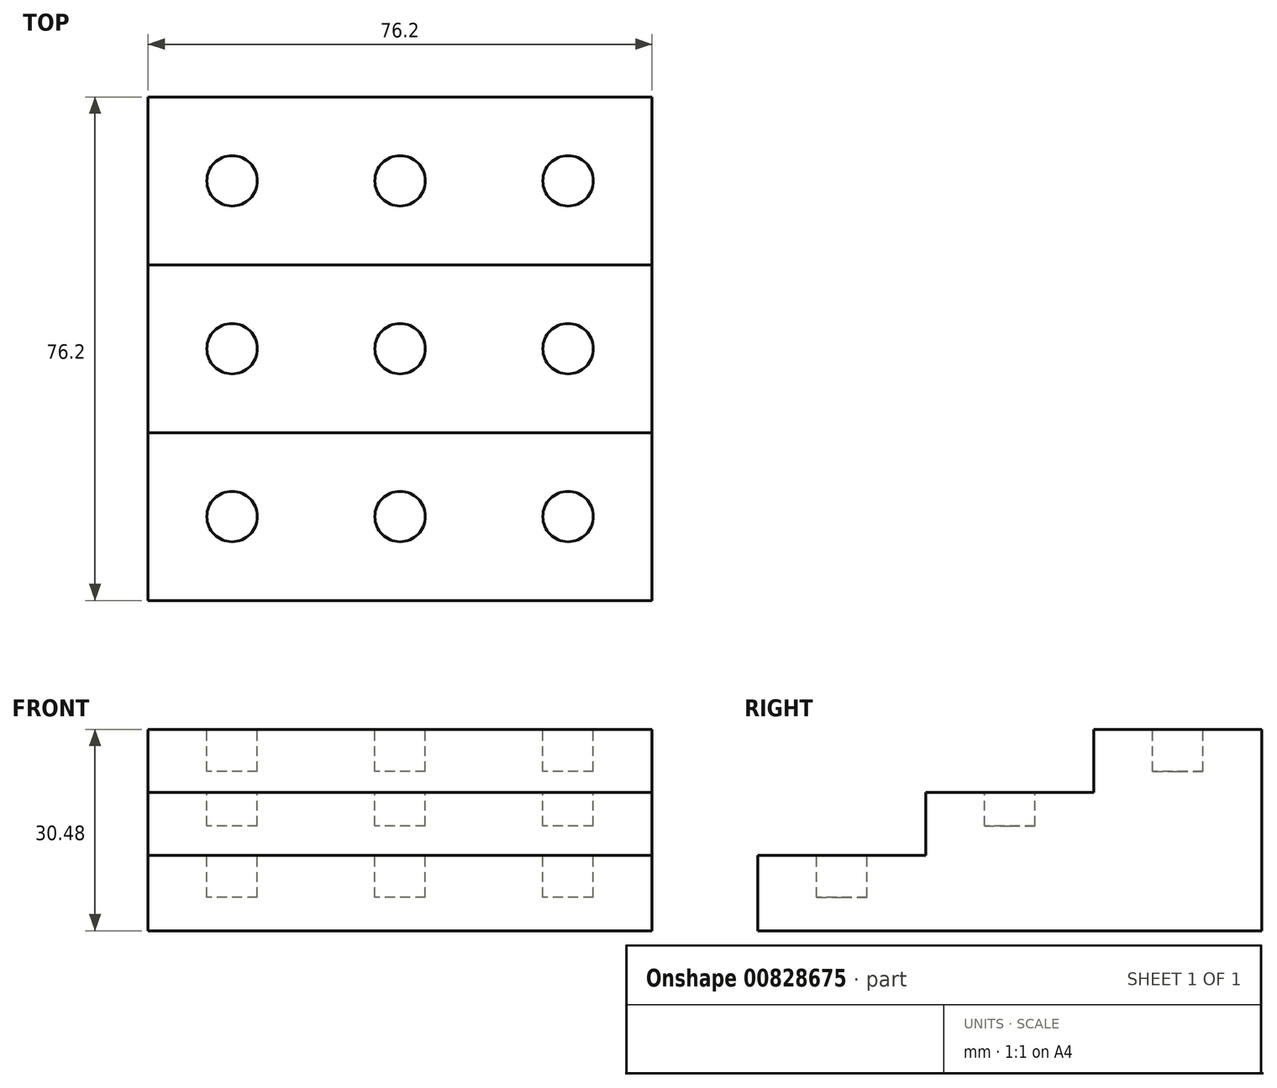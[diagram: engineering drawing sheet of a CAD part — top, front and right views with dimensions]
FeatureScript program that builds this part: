
annotation { "Feature Type Name" : "Feature", "Feature Type Description" : "" }
export const myFeature = defineFeature(function(context is Context, id is Id, definition is map)
    precondition{}
    {
        {
            var Q0;
            Q0=qCreatedBy(makeId("Top.planeOp"),FACE);
            var sketch = newSketch(context, id + "F0", { "sketchPlane" : qUnion([Q0])});
            skLineSegment(sketch, "E0", {"start": v(0, 0) * mm, "end": v(0, 25.4) * mm});
            skLineSegment(sketch, "E1", {"start": v(0, 25.4) * mm, "end": v(76.2, 25.4) * mm});
            skLineSegment(sketch, "E2", {"start": v(76.2, 25.4) * mm, "end": v(76.2, 0) * mm});
            skLineSegment(sketch, "E3", {"start": v(76.2, 0) * mm, "end": v(0, 0) * mm});
            skSolve(sketch);
        }
        {
            var Q0;
            Q0=qSketchRegion(id+"F0",true);
            extrude(context, id + "F1", {"entities" : qUnion([Q0]), "depth" : 11.43 * mm, "offsetDistance" : 25.4 * mm});
        }
        {
            var Q0;
            Q0=makeQuery(id+"F1.opExtrude","CAP_FACE",FACE,{"disambiguationData":[OSD([sQuery(id+"F0.wireOp",EDGE,"E0"),sQuery(id+"F0.wireOp",EDGE,"E1"),sQuery(id+"F0.wireOp",EDGE,"E2"),sQuery(id+"F0.wireOp",EDGE,"E3")])],"isStart":false});
            var sketch = newSketch(context, id + "F2", { "sketchPlane" : qUnion([Q0])});
            skCircle(sketch, "E4", {"center": v(12.7, 12.7) * mm, "radius": 3.81 * mm});
            skCircle(sketch, "E5", {"center": v(38.1, 12.7) * mm, "radius": 3.81 * mm});
            skCircle(sketch, "E6", {"center": v(63.5, 12.7) * mm, "radius": 3.81 * mm});
            skSolve(sketch);
        }
        {
            var Q0;
            Q0=qSketchRegion(id+"F2",true);
            extrude(context, id + "F3", {"entities" : qUnion([Q0]), "operationType" : NewBodyOperationType.REMOVE, "oppositeDirection" : true, "depth" : 6.35 * mm, "offsetDistance" : 25.4 * mm});
        }
        {
            var Q0;
            Q0=makeQuery(id+"F1.opExtrude","SWEPT_FACE",FACE,{"disambiguationData":[OSD([sQuery(id+"F0.wireOp",EDGE,"E1")])]});
            var sketch = newSketch(context, id + "F4", { "sketchPlane" : qUnion([Q0])});
            skSolve(sketch);
        }
        {
            var Q0;
            Q0 = qSketchRegion(id + "F4", true);
            var Q1;
            {var subQ0=sQuery(id+"F0.wireOp",EDGE,"E1");Q1=makeQuery(id+"F4.imprint","IMPRINT",FACE,{"disambiguationData":[TD([[makeQuery(id+"F4.imprint","IMPRINT",EDGE,{"derivedFrom":makeQuery(id+"F1.opExtrude","CAP_EDGE",EDGE,{"disambiguationData":[OSD([subQ0])],"isStart":true})}),-1.0]])]});}
            extrude(context, id + "F5", {"entities" : qUnion([Q0, Q1]), "operationType" : NewBodyOperationType.ADD, "depth" : 25.4 * mm, "offsetDistance" : 25.4 * mm});
        }
        {
            var Q0;
            {var subQ0=sQuery(id+"F0.wireOp",EDGE,"E1");Q0=makeQuery(id+"F5.boolean.opBoolean","MERGE",FACE,{"derivedFrom":[makeQuery(id+"F1.opExtrude","CAP_FACE",FACE,{"disambiguationData":[OSD([sQuery(id+"F0.wireOp",EDGE,"E0"),subQ0,sQuery(id+"F0.wireOp",EDGE,"E2"),sQuery(id+"F0.wireOp",EDGE,"E3")])],"isStart":false}),makeQuery(id+"F5.opExtrude","SWEPT_FACE",FACE,{"disambiguationData":[OSD([subQ0]),TDD([makeQuery(id+"F4.imprint","IMPRINT",EDGE,{"derivedFrom":makeQuery(id+"F1.opExtrude","CAP_EDGE",EDGE,{"disambiguationData":[OSD([subQ0])],"isStart":false})})])]})]});}
            var sketch = newSketch(context, id + "F6", { "sketchPlane" : qUnion([Q0])});
            skLineSegment(sketch, "E7", {"start": v(76.2, 25.4) * mm, "end": v(0, 25.4) * mm});
            skSolve(sketch);
        }
        {
            var Q0;
            Q0 = qSketchRegion(id + "F6", true);
            var Q1;
            {var subQ0=sQuery(id+"F6.wireOp",EDGE,"E7");Q1=makeQuery(id+"F6.imprint","IMPRINT",FACE,{"disambiguationData":[TD([[makeQuery(id+"F6.imprint","IMPRINT",EDGE,{"derivedFrom":subQ0}),-1.0]])]});}
            extrude(context, id + "F7", {"entities" : qUnion([Q0, Q1]), "operationType" : NewBodyOperationType.ADD, "depth" : 9.52 * mm, "offsetDistance" : 25.4 * mm});
        }
        {
            var Q0;
            {var subQ0=sQuery(id+"F0.wireOp",EDGE,"E1");Q0=makeQuery(id+"F7.boolean.opBoolean","MERGE",FACE,{"derivedFrom":[makeQuery(id+"F5.opExtrude","CAP_FACE",FACE,{"disambiguationData":[OSD([sQuery(id+"F0.wireOp",EDGE,"E0"),subQ0,sQuery(id+"F0.wireOp",EDGE,"E2")])],"isStart":false}),makeQuery(id+"F7.opExtrude","SWEPT_FACE",FACE,{"disambiguationData":[OSD([subQ0])]})]});}
            var sketch = newSketch(context, id + "F8", { "sketchPlane" : qUnion([Q0])});
            skSolve(sketch);
        }
        {
            var Q0;
            {var subQ0=sQuery(id+"F0.wireOp",EDGE,"E1");Q0=makeQuery(id+"F8.imprint","IMPRINT",FACE,{"disambiguationData":[TD([[makeQuery(id+"F8.imprint","IMPRINT",EDGE,{"derivedFrom":makeQuery(id+"F7.opExtrude","CAP_EDGE",EDGE,{"disambiguationData":[OSD([subQ0])],"isStart":false})}),1.0]])]});}
            extrude(context, id + "F9", {"entities" : qUnion([Q0]), "operationType" : NewBodyOperationType.ADD, "depth" : 25.4 * mm, "offsetDistance" : 25.4 * mm});
        }
        {
            var Q0;
            {var subQ0=sQuery(id+"F0.wireOp",EDGE,"E1");Q0=makeQuery(id+"F9.boolean.opBoolean","MERGE",FACE,{"derivedFrom":[makeQuery(id+"F7.opExtrude","CAP_FACE",FACE,{"disambiguationData":[OSD([sQuery(id+"F0.wireOp",EDGE,"E0"),subQ0,sQuery(id+"F0.wireOp",EDGE,"E2"),sQuery(id+"F6.wireOp",EDGE,"E7")])],"isStart":false}),makeQuery(id+"F9.opExtrude","SWEPT_FACE",FACE,{"disambiguationData":[OSD([subQ0]),TDD([makeQuery(id+"F8.imprint","IMPRINT",EDGE,{"derivedFrom":makeQuery(id+"F7.opExtrude","CAP_EDGE",EDGE,{"disambiguationData":[OSD([subQ0])],"isStart":false})})])]})]});}
            var sketch = newSketch(context, id + "F10", { "sketchPlane" : qUnion([Q0])});
            skLineSegment(sketch, "E8", {"start": v(76.2, 50.8) * mm, "end": v(0, 50.8) * mm});
            skSolve(sketch);
        }
        {
            var Q0;
            {var subQ0=sQuery(id+"F10.wireOp",EDGE,"E8");Q0=makeQuery(id+"F10.imprint","IMPRINT",FACE,{"disambiguationData":[TD([[makeQuery(id+"F10.imprint","IMPRINT",EDGE,{"derivedFrom":subQ0}),-1.0]])]});}
            extrude(context, id + "F11", {"entities" : qUnion([Q0]), "operationType" : NewBodyOperationType.ADD, "depth" : 9.52 * mm, "offsetDistance" : 25.4 * mm});
        }
        {
            var Q0;
            {var subQ0=sQuery(id+"F0.wireOp",EDGE,"E1");Q0=makeQuery(id+"F9.boolean.opBoolean","MERGE",FACE,{"derivedFrom":[makeQuery(id+"F7.opExtrude","CAP_FACE",FACE,{"disambiguationData":[OSD([sQuery(id+"F0.wireOp",EDGE,"E0"),subQ0,sQuery(id+"F0.wireOp",EDGE,"E2"),sQuery(id+"F6.wireOp",EDGE,"E7")])],"isStart":false}),makeQuery(id+"F9.opExtrude","SWEPT_FACE",FACE,{"disambiguationData":[OSD([subQ0]),TDD([makeQuery(id+"F8.imprint","IMPRINT",EDGE,{"derivedFrom":makeQuery(id+"F7.opExtrude","CAP_EDGE",EDGE,{"disambiguationData":[OSD([subQ0])],"isStart":false})})])]})]});}
            var sketch = newSketch(context, id + "F12", { "sketchPlane" : qUnion([Q0])});
            skCircle(sketch, "E9", {"center": v(12.7, 38.1) * mm, "radius": 3.81 * mm});
            skCircle(sketch, "E10", {"center": v(38.1, 38.1) * mm, "radius": 3.81 * mm});
            skCircle(sketch, "E11", {"center": v(63.5, 38.1) * mm, "radius": 3.81 * mm});
            skSolve(sketch);
        }
        {
            var Q0;
            Q0 = qSketchRegion(id + "F12", true);
            extrude(context, id + "F13", {"entities" : qUnion([Q0]), "operationType" : NewBodyOperationType.REMOVE, "oppositeDirection" : true, "depth" : 5.08 * mm, "offsetDistance" : 25.4 * mm});
        }
        {
            var Q0;
            Q0=makeQuery(id+"F11.opExtrude","CAP_FACE",FACE,{"disambiguationData":[OSD([sQuery(id+"F0.wireOp",EDGE,"E0"),sQuery(id+"F0.wireOp",EDGE,"E1"),sQuery(id+"F0.wireOp",EDGE,"E2"),sQuery(id+"F10.wireOp",EDGE,"E8")])],"isStart":false});
            var sketch = newSketch(context, id + "F14", { "sketchPlane" : qUnion([Q0])});
            skCircle(sketch, "E12", {"center": v(12.7, 63.5) * mm, "radius": 3.81 * mm});
            skCircle(sketch, "E13", {"center": v(38.1, 63.5) * mm, "radius": 3.81 * mm});
            skCircle(sketch, "E14", {"center": v(63.5, 63.5) * mm, "radius": 3.81 * mm});
            skSolve(sketch);
        }
        {
            var Q0;
            Q0=makeQuery(id+"F14.imprint","IMPRINT",FACE,{"disambiguationData":[TD([[makeQuery(id+"F14.imprint","IMPRINT",EDGE,{"derivedFrom":sQuery(id+"F14.wireOp",EDGE,"E12")}),1.0]])]});
            var Q1;
            Q1=makeQuery(id+"F14.imprint","IMPRINT",FACE,{"disambiguationData":[TD([[makeQuery(id+"F14.imprint","IMPRINT",EDGE,{"derivedFrom":sQuery(id+"F14.wireOp",EDGE,"E13")}),1.0]])]});
            var Q2;
            Q2=makeQuery(id+"F14.imprint","IMPRINT",FACE,{"disambiguationData":[TD([[makeQuery(id+"F14.imprint","IMPRINT",EDGE,{"derivedFrom":sQuery(id+"F14.wireOp",EDGE,"E14")}),1.0]])]});
            extrude(context, id + "F15", {"entities" : qUnion([Q0, Q1, Q2]), "operationType" : NewBodyOperationType.REMOVE, "oppositeDirection" : true, "depth" : 6.35 * mm, "offsetDistance" : 25.4 * mm});
        }
    });
